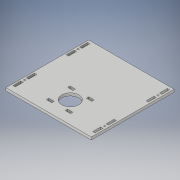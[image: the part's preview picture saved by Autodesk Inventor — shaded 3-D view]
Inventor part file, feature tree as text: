
AUTODESK INVENTOR PART (.ipt)
format: ipt  version: 2018 (Build 220112000, 112)  size: 180,224 bytes
history: native  units: in
note: dims shown in document units (in); Inventor stores cm internally (conversion verified against a paired STEP export)
features: extrude x2, sketch x2
ambient origin geometry x8: Origin, YZ Plane, XZ Plane, XY Plane, X Axis, Y Axis, Z Axis, Center Point
bodies: Solid1 (feature_tree)
feature tree (4):
  extrude  "Extrusion1"  Depth=7.75in
  extrude  "Extrusion2"  Depth=0.75in
  sketch  "Sketch1"  dims[d0=8.0in d1=7.75in]
  sketch  "Sketch2"  dims[d7=0.156in d9=0.75in d11=0.25in d12=0.0in d13=1.1417in d15=4.0551in d16=1.1417in d17=0.628in d20=0.628in d23=0.628in d29=1.2205in d30=0.8071in d31=1.6142in d32=0.25in d33=0.0in d34=0.219in d35=0.219in d37=0.219in]
